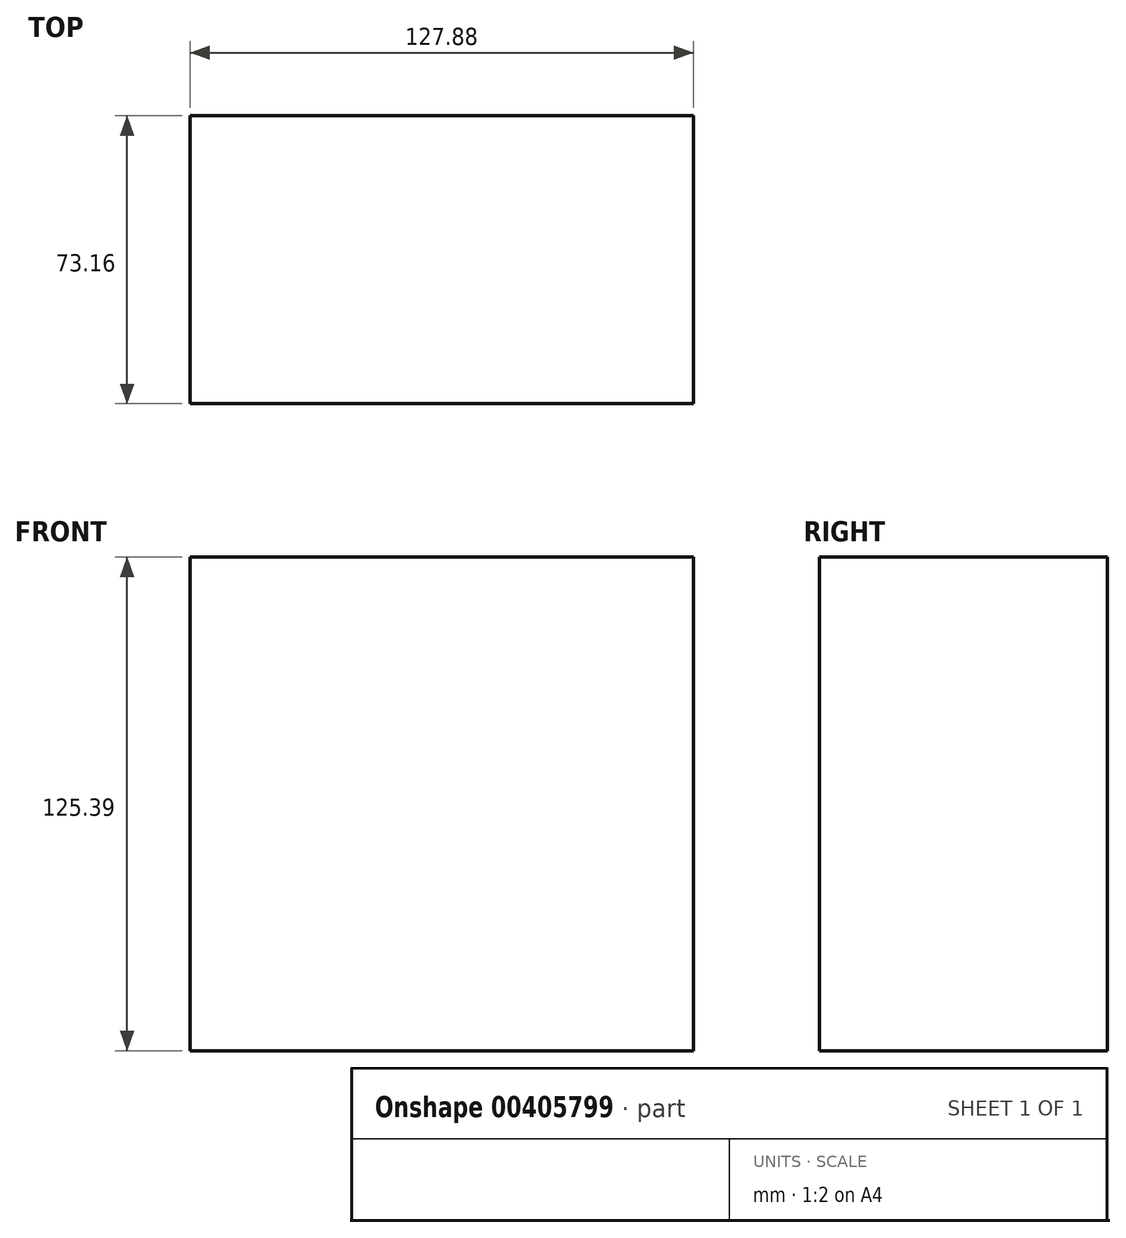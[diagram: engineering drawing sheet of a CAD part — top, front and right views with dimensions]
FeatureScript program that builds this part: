
annotation { "Feature Type Name" : "Feature", "Feature Type Description" : "" }
export const myFeature = defineFeature(function(context is Context, id is Id, definition is map)
    precondition{}
    {
        {
            var Q0;
            Q0=qCreatedBy(makeId("Front.planeOp"),FACE);
            var sketch = newSketch(context, id + "F0", { "sketchPlane" : qUnion([Q0])});
            skLineSegment(sketch, "E0.bottom", {"start": v(61.35, 55.7) * mm, "end": v(-66.53, 55.7) * mm});
            skLineSegment(sketch, "E0.top", {"start": v(61.35, -69.69) * mm, "end": v(-66.53, -69.69) * mm});
            skLineSegment(sketch, "E0.left", {"start": v(61.35, 55.7) * mm, "end": v(61.35, -69.69) * mm});
            skLineSegment(sketch, "E0.right", {"start": v(-66.53, 55.7) * mm, "end": v(-66.53, -69.69) * mm});
            skSolve(sketch);
        }
        {
            var Q0;
            Q0=makeQuery(id+"F0.imprint","IMPRINT",FACE,{"disambiguationData":[TD([[makeQuery(id+"F0.imprint","IMPRINT",EDGE,{"derivedFrom":sQuery(id+"F0.wireOp",EDGE,"E0.bottom")}),1.0]])]});
            extrude(context, id + "F1", {"entities" : qUnion([Q0]), "depth" : 73.16 * mm});
        }
    });
